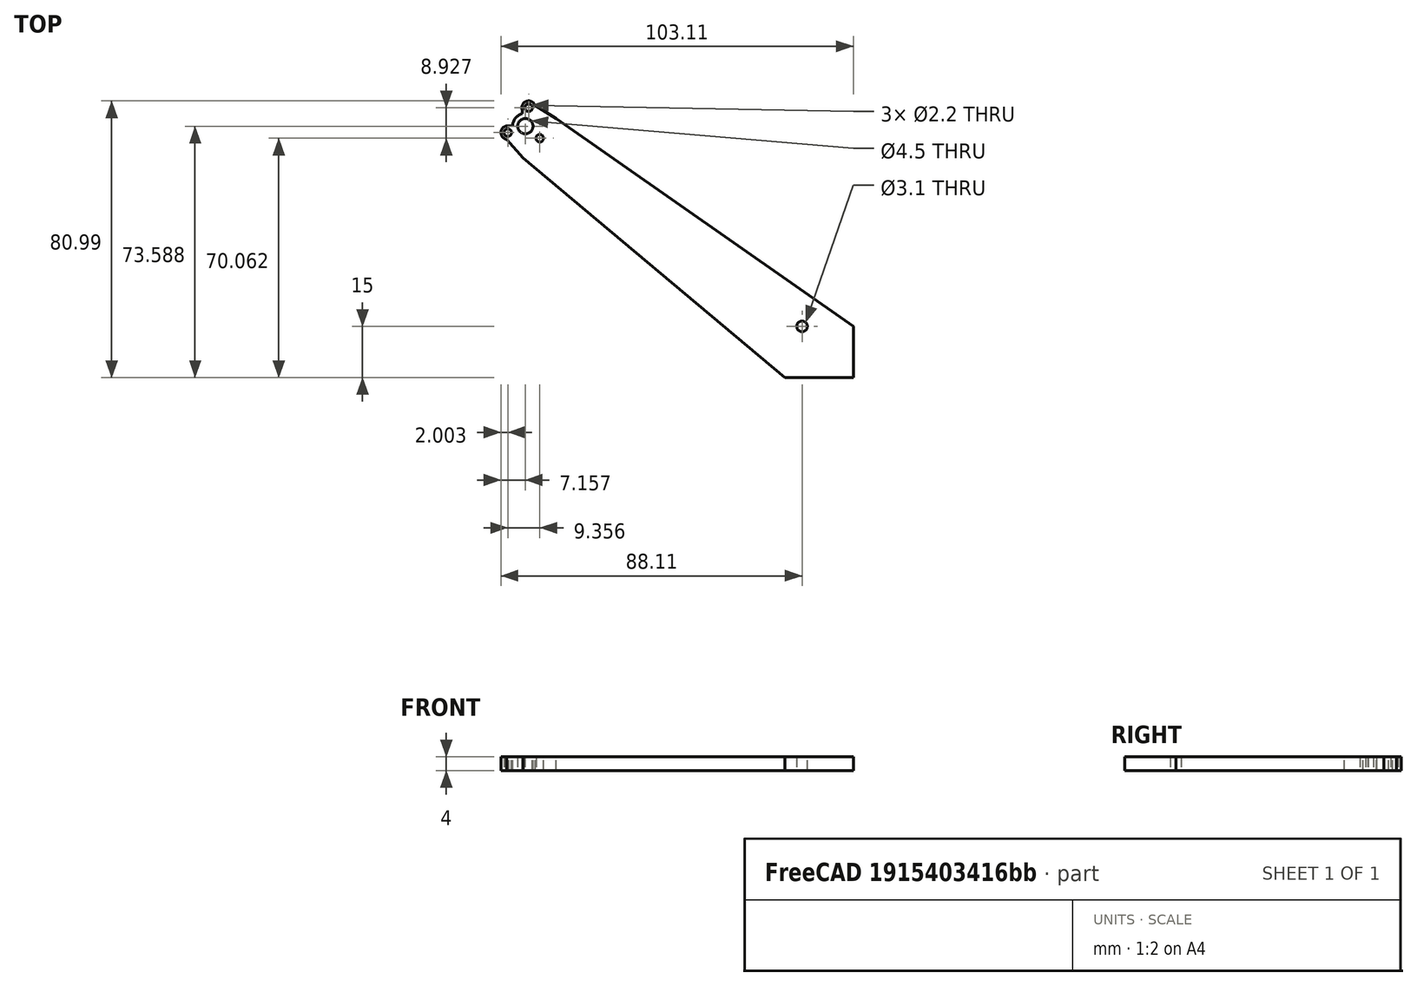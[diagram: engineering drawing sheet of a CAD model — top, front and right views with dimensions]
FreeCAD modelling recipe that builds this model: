
FCSTD DOCUMENT  (FreeCAD 0.20R29410 (Git))
Label: arm
License: All rights reserved
LicenseURL: http://en.wikipedia.org/wiki/All_rights_reserved
objects: PartDesign::CoordinateSystem×4, Sketcher::SketchObject×1, PartDesign::Pad×1, PartDesign::Body×1
note: 8 computed .brp shape members not serialized (recipe doc carries the construction recipe); baked Part::Feature solids carry a one-line shape summary decoded from their .brp

FEATURE [Sketcher::SketchObject] Sketch
  FullyConstrained = true
  MapMode = 5
  Support = -> [XY_Plane]
  sketch-geometry (22):
    g0: LineSegment StartX=-20 StartY=0 StartZ=0 EndX=0 EndY=0 EndZ=0
    g1: LineSegment StartX=0 StartY=0 StartZ=0 EndX=0 EndY=15 EndZ=0
    g2: LineSegment StartX=-20 StartY=0 StartZ=0 EndX=-96.6044 EndY=64.2788 EndZ=0
    g3: LineSegment StartX=0 StartY=15 StartZ=0 EndX=-86.8979 EndY=75.8466 EndZ=0
    g4: LineSegment StartX=-96.6044 StartY=64.2788 StartZ=0 EndX=-86.8979 EndY=75.8466 EndZ=0
    g5: LineSegment StartX=-91.7514 StartY=70.0624 StartZ=0 EndX=-95.0006 EndY=78.9895 EndZ=0
    g6: LineSegment StartX=-95.0006 StartY=78.9895 StartZ=0 EndX=-101.107 EndY=71.7121 EndZ=0
    g7: LineSegment StartX=-101.107 StartY=71.7121 StartZ=0 EndX=-91.7514 EndY=70.0624 EndZ=0
    g8: Circle CenterX=-95.953 CenterY=73.588 CenterZ=0 NormalX=0 NormalY=0 NormalZ=1 AngleXU=0 Radius=5.48483
    g9: Circle CenterX=-91.7514 CenterY=70.0624 CenterZ=0 NormalX=0 NormalY=0 NormalZ=1 AngleXU=0 Radius=1.1
    g10: Circle CenterX=-95.0006 CenterY=78.9895 CenterZ=0 NormalX=0 NormalY=0 NormalZ=1 AngleXU=0 Radius=1.1
    g11: Circle CenterX=-101.107 CenterY=71.7121 CenterZ=0 NormalX=0 NormalY=0 NormalZ=1 AngleXU=0 Radius=1.1
    g12: ArcOfCircle CenterX=-95.953 CenterY=73.588 CenterZ=0 NormalX=0 NormalY=0 NormalZ=1 AngleXU=0 Radius=3.75 StartAngle=1.79996 EndAngle=3.08696
    g13: ArcOfCircle CenterX=-95.0006 CenterY=78.9895 CenterZ=0 NormalX=0 NormalY=0 NormalZ=1 AngleXU=0 Radius=2 StartAngle=0.311549 EndAngle=3.45314
    g14: ArcOfCircle CenterX=-101.107 CenterY=71.7121 CenterZ=0 NormalX=0 NormalY=0 NormalZ=1 AngleXU=0 Radius=2 StartAngle=1.43378 EndAngle=4.57537
    g15: LineSegment StartX=-96.8049 StartY=77.2399 StartZ=0 EndX=-96.9043 EndY=78.3764 EndZ=0
    g16: LineSegment StartX=-99.6974 StartY=73.7927 StartZ=0 EndX=-100.834 EndY=73.6933 EndZ=0
    g17: LineSegment StartX=-99.6974 StartY=73.7927 StartZ=0 EndX=-96.8049 EndY=77.2399 EndZ=0
    g18: LineSegment StartX=-86.8979 StartY=75.8466 StartZ=0 EndX=-93.0969 EndY=79.6025 EndZ=0
    g19: LineSegment StartX=-96.6044 StartY=64.2788 StartZ=0 EndX=-101.38 EndY=69.7308 EndZ=0
    g20: Circle CenterX=-95.953 CenterY=73.588 CenterZ=0 NormalX=0 NormalY=0 NormalZ=1 AngleXU=0 Radius=2.25
    g21: Circle CenterX=-15 CenterY=15 CenterZ=0 NormalX=0 NormalY=0 NormalZ=1 AngleXU=0 Radius=1.55
  constraints (59):
    c: PointOnObject(g0,g-1)
    c: Coincident(g0,g-1)
    c: Coincident(g1,g0)
    c: PointOnObject(g1,g-2)
    c: Coincident(g2,g0)
    c: Coincident(g3,g1)
    c: DistanceY(g1,g1) = 15
    c: DistanceX(g0,g0) = 20
    c: Angle(g-1,g2) = 2.44346
    c: Coincident(g4,g2)
    c: Coincident(g4,g3)
    c: Angle(g2,g4) = 1.5708
    c: Angle(g2,g3) = 0.0872665
    c: Distance(g2) = 100
    c: Coincident(g5,g6)
    c: Coincident(g6,g7)
    c: Coincident(g7,g5)
    c: Equal(g5,g6)
    c: Equal(g5,g7)
    c: PointOnObject(g5,g8)
    c: PointOnObject(g6,g8)
    c: PointOnObject(g7,g8)
    c: PointOnObject(g5,g4)
    c: Parallel(g6,g4)
    c: Distance(g5,g2) = 7.55
    c: Coincident(g9,g5)
    c: Coincident(g10,g5)
    c: Coincident(g11,g6)
    c: Equal(g10,g11)
    c: Equal(g10,g9)
    c: Diameter(g10) = 2.2
    c: Distance(g7) = 9.5
    c: Coincident(g12,g8)
    c: Diameter(g12) = 7.5
    c: Coincident(g13,g10)
    c: Coincident(g14,g11)
    c: Diameter(g14) = 4
    c: Diameter(g13) = 4
    c: Angle(g14) = 3.14159
    c: Angle(g13) = 3.14159
    c: Coincident(g15,g12)
    c: Coincident(g15,g13)
    c: Coincident(g16,g12)
    c: Coincident(g16,g14)
    c: Angle(g15,g16) = 1.5708
    c: Equal(g16,g15)
    c: Coincident(g17,g12)
    c: Coincident(g17,g12)
    c: Parallel(g17,g4)
    c: Distance(g17) = 4.5
    c: Coincident(g18,g3)
    c: Coincident(g18,g13)
    c: Coincident(g19,g2)
    c: Coincident(g19,g14)
    c: Coincident(g20,g12)
    c: Diameter(g20) = 4.5
    c: Diameter(g21) = 3.1
    c: DistanceX(g21,g0) = 15
    c: DistanceY(g0,g21) = 15
FEATURE [PartDesign::Pad] Pad
  Direction = (0,0,1)
  Length = 4
  Length2 = 10
  Profile = -> Sketch
  ReferenceAxis = -> Sketch [N_Axis]
  Type = 0
FEATURE [PartDesign::CoordinateSystem] LCS_1  label="LCS_L"
  AttacherType = Attacher::AttachEngine3D
  AttachmentOffset = pos=(0,0,0) rot=(0,0,1;0.872665rad)
  MapMode = 11
  Placement = pos=(-95.953,73.588,4) rot=(0,0,1;2.44346rad)
  Support = -> [Pad]
FEATURE [PartDesign::CoordinateSystem] LCS_R
  AttacherType = Attacher::AttachEngine3D
  AttachmentOffset = pos=(0,0,0) rot=(0,0,1;0.872665rad)
  MapMode = 11
  Placement = pos=(-95.953,73.588,0) rot=(0,0,1;2.44346rad)
  Support = -> [Pad]
FEATURE [PartDesign::CoordinateSystem] LCS_IL
  AttacherType = Attacher::AttachEngine3D
  MapMode = 11
  Placement = pos=(-15,15,4) rot=(0,0,1;1.5708rad)
  Support = -> [Pad]
FEATURE [PartDesign::CoordinateSystem] LCS_IR
  AttacherType = Attacher::AttachEngine3D
  MapMode = 11
  Placement = pos=(-15,15,0) rot=(0,0,1;1.5708rad)
  Support = -> [Pad]
FEATURE [PartDesign::Body] Body
  Group = -> [Sketch,Pad,LCS_1,LCS_R,LCS_IL,LCS_IR]
  Origin = -> Origin
  Tip = -> Pad
